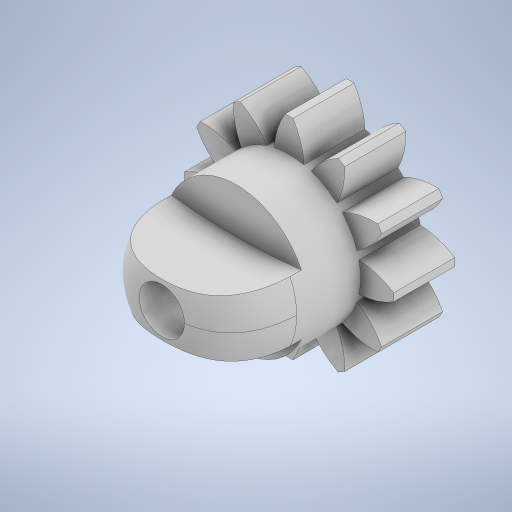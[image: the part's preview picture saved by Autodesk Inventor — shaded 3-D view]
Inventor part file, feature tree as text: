
AUTODESK INVENTOR PART (.ipt)
format: ipt  version: 2023.1 (Build 271208000, 208)  size: 435,712 bytes
history: native  units: mm
features: extrude x8, sketch x6, other x1, pattern_circular x1, revolve x1, projected_geometry x1
ambient origin geometry x8: Origin, YZ Plane, XZ Plane, XY Plane, X Axis, Y Axis, Z Axis, Center Point
bodies: Body1 (feature_tree)
feature tree (18):
  other  "솔리드1"
  sketch  "스케치1"
  extrude  "돌출1"  Depth=24.0mm
  extrude  "돌출2"  Depth=28.0mm
  extrude  "돌출3"  Depth=19.0mm
  extrude  "돌출4"  Depth=1.57mm
  extrude  "돌출6"  Depth=1.0mm
  pattern_circular  "원형 패턴2"  [2 undecoded]
  sketch  "스케치5"
  extrude  "돌출7"  Depth=7.5mm
  extrude  "돌출8"  Depth=4.9mm
  extrude  "돌출9"  Depth=8.1mm TaperAngle=0.0deg
  revolve  "회전1"
  sketch  "스케치2"
  sketch  "스케치4"
  projected_geometry  "투영된 루프2"
  sketch  "스케치6"
  sketch  "스케치7"
note: 2 required parameter values undecoded (feature->parameter linkage not recoverable at this tier; creation-order binding heuristic only, values carry confidence <= 0.55)
